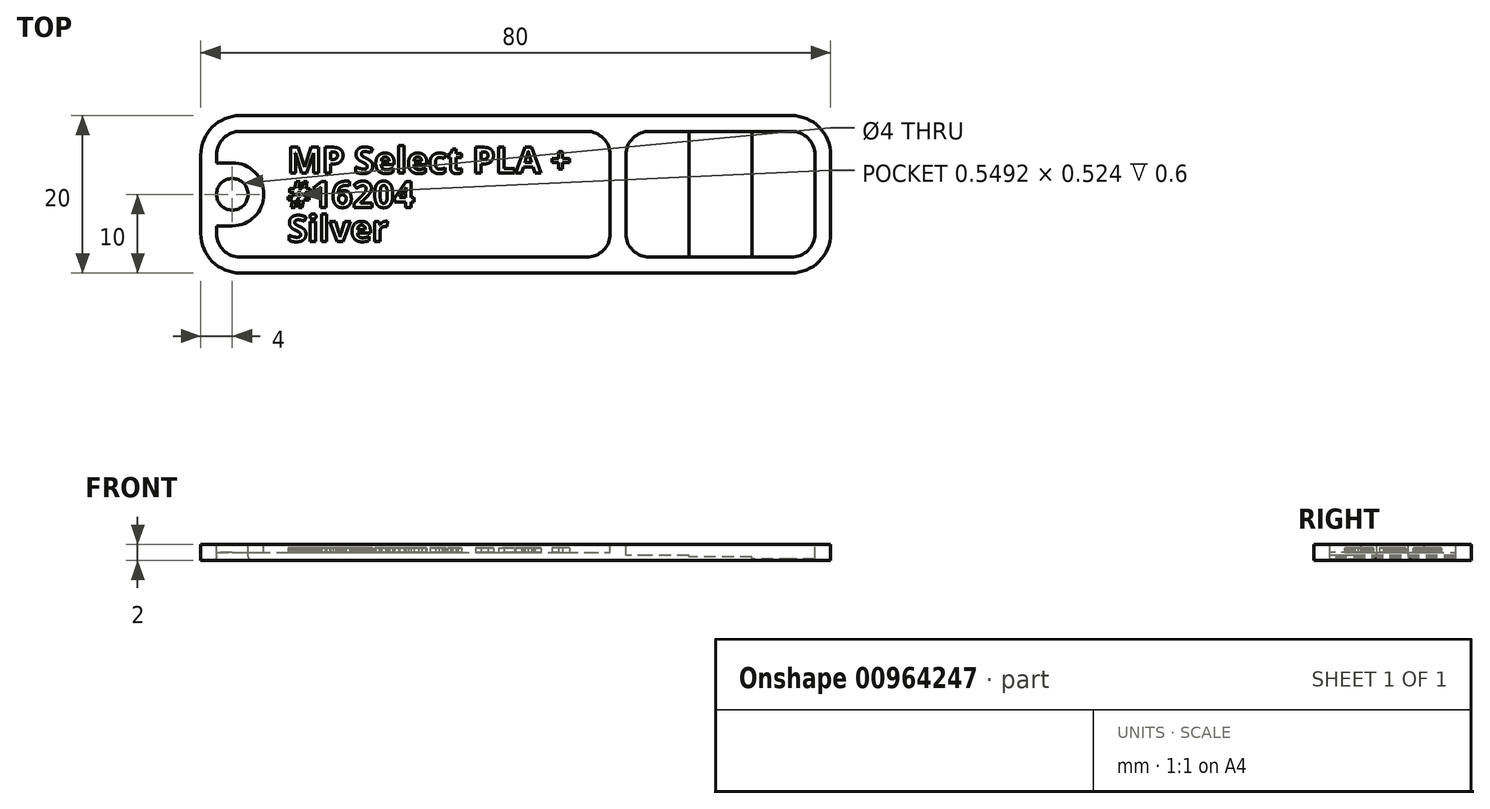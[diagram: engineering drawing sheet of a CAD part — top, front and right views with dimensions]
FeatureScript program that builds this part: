
annotation { "Feature Type Name" : "Feature", "Feature Type Description" : "" }
export const myFeature = defineFeature(function(context is Context, id is Id, definition is map)
    precondition{}
    {
        {
            var Q0;
            Q0=qCreatedBy(makeId("Top.planeOp"),FACE);
            var sketch = newSketch(context, id + "F0", { "sketchPlane" : qUnion([Q0])});
            skLineSegment(sketch, "E0.bottom", {"start": v(35, 10) * mm, "end": v(-35, 10) * mm});
            skLineSegment(sketch, "E0.top", {"start": v(35, -10) * mm, "end": v(-35, -10) * mm});
            skLineSegment(sketch, "E0.left", {"start": v(40, 5) * mm, "end": v(40, -5) * mm});
            skLineSegment(sketch, "E0.right", {"start": v(-40, 5) * mm, "end": v(-40, -5) * mm});
            skPoint(sketch, "E0.middle", {"position": v(0, 0) * mm});
            skPoint(sketch, "E1.visualSharp", {"position": v(-40, 10) * mm});
            skArc(sketch, "E1.filletArc", {"start": v(-35, 10) * mm, "mid": v(-38.54, 8.54) * mm, "end": v(-40, 5) * mm});
            skPoint(sketch, "E2.visualSharp", {"position": v(40, 10) * mm});
            skArc(sketch, "E2.filletArc", {"start": v(40, 5) * mm, "mid": v(38.54, 8.54) * mm, "end": v(35, 10) * mm});
            skPoint(sketch, "E3.visualSharp", {"position": v(40, -10) * mm});
            skArc(sketch, "E3.filletArc", {"start": v(35, -10) * mm, "mid": v(38.54, -8.54) * mm, "end": v(40, -5) * mm});
            skPoint(sketch, "E4.visualSharp", {"position": v(-40, -10) * mm});
            skArc(sketch, "E4.filletArc", {"start": v(-40, -5) * mm, "mid": v(-38.54, -8.54) * mm, "end": v(-35, -10) * mm});
            skSolve(sketch);
        }
        {
            var Q0;
            Q0=qSketchRegion(id+"F0",true);
            extrude(context, id + "F1", {"entities" : qUnion([Q0]), "offsetDistance" : 25 * mm, "depth" : 2 * mm});
        }
        {
            var Q0;
            Q0=makeQuery(id+"F1.opExtrude","CAP_FACE",FACE,{"disambiguationData":[OSD([sQuery(id+"F0.wireOp",EDGE,"E0.bottom"),sQuery(id+"F0.wireOp",EDGE,"E0.top"),sQuery(id+"F0.wireOp",EDGE,"E0.left"),sQuery(id+"F0.wireOp",EDGE,"E0.right"),sQuery(id+"F0.wireOp",EDGE,"E1.filletArc"),sQuery(id+"F0.wireOp",EDGE,"E2.filletArc"),sQuery(id+"F0.wireOp",EDGE,"E3.filletArc"),sQuery(id+"F0.wireOp",EDGE,"E4.filletArc")])],"isStart":false});
            var sketch = newSketch(context, id + "F2", { "sketchPlane" : qUnion([Q0])});
            skLineSegment(sketch, "E5.0", {"start": v(38, -5) * mm, "end": v(38, 5) * mm});
            skArc(sketch, "E5.1", {"start": v(35, -8) * mm, "mid": v(37.12, -7.12) * mm, "end": v(38, -5) * mm});
            skArc(sketch, "E5.2", {"start": v(38, 5) * mm, "mid": v(37.12, 7.12) * mm, "end": v(35, 8) * mm});
            skLineSegment(sketch, "E5.3", {"start": v(-35, -8) * mm, "end": v(9, -8) * mm});
            skLineSegment(sketch, "E5.4", {"start": v(35, 8) * mm, "end": v(17, 8) * mm});
            skArc(sketch, "E5.5", {"start": v(-35, 8) * mm, "mid": v(-37.12, 7.12) * mm, "end": v(-38, 5) * mm});
            skArc(sketch, "E5.7", {"start": v(-38, -5) * mm, "mid": v(-37.12, -7.12) * mm, "end": v(-35, -8) * mm});
            skCircle(sketch, "E6", {"center": v(-36, 0) * mm, "radius": 2 * mm, "construction": true});
            skArc(sketch, "E7.0", {"start": v(-36, -4) * mm, "mid": v(-32, 0) * mm, "end": v(-36, 4) * mm});
            skLineSegment(sketch, "E8", {"start": v(-38, -5) * mm, "end": v(-38, -4) * mm});
            skLineSegment(sketch, "E9", {"start": v(-36, 4) * mm, "end": v(-38, 4) * mm});
            skLineSegment(sketch, "E10", {"start": v(-36, -4) * mm, "end": v(-38, -4) * mm});
            skLineSegment(sketch, "E11.trimOffspring", {"start": v(-38, 4) * mm, "end": v(-38, 5) * mm});
            skArc(sketch, "E12", {"start": v(17, 8) * mm, "mid": v(14.88, 7.12) * mm, "end": v(14, 5) * mm});
            skArc(sketch, "E13", {"start": v(14, -5) * mm, "mid": v(14.88, -7.12) * mm, "end": v(17, -8) * mm});
            skLineSegment(sketch, "E14", {"start": v(14, -5) * mm, "end": v(14, 5) * mm});
            skArc(sketch, "E15", {"start": v(12, 5) * mm, "mid": v(11.12, 7.12) * mm, "end": v(9, 8) * mm});
            skArc(sketch, "E16", {"start": v(12, -5) * mm, "mid": v(11.12, -7.12) * mm, "end": v(9, -8) * mm});
            skLineSegment(sketch, "E17", {"start": v(12, -5) * mm, "end": v(12, 5) * mm});
            skLineSegment(sketch, "E18.trimOffspring", {"start": v(9, 8) * mm, "end": v(-35, 8) * mm});
            skLineSegment(sketch, "E19.trimOffspring", {"start": v(17, -8) * mm, "end": v(35, -8) * mm});
            skSolve(sketch);
        }
        {
            var Q0;
            Q0=qSketchRegion(id+"F2",true);
            extrude(context, id + "F3", {"entities" : qUnion([Q0]), "operationType" : NewBodyOperationType.REMOVE, "oppositeDirection" : true, "offsetDistance" : 25 * mm, "depth" : 1 * mm});
        }
        {
            var Q0;
            Q0=makeQuery(id+"F1.opExtrude","CAP_FACE",FACE,{"disambiguationData":[OSD([sQuery(id+"F0.wireOp",EDGE,"E0.bottom"),sQuery(id+"F0.wireOp",EDGE,"E0.top"),sQuery(id+"F0.wireOp",EDGE,"E0.left"),sQuery(id+"F0.wireOp",EDGE,"E0.right"),sQuery(id+"F0.wireOp",EDGE,"E1.filletArc"),sQuery(id+"F0.wireOp",EDGE,"E2.filletArc"),sQuery(id+"F0.wireOp",EDGE,"E3.filletArc"),sQuery(id+"F0.wireOp",EDGE,"E4.filletArc")])],"isStart":false});
            var sketch = newSketch(context, id + "F4", { "sketchPlane" : qUnion([Q0])});
            skCircle(sketch, "E20.0", {"center": v(-36, 0) * mm, "radius": 2 * mm});
            skSolve(sketch);
        }
        {
            var Q0;
            Q0=qSketchRegion(id+"F4",true);
            extrude(context, id + "F5", {"entities" : qUnion([Q0]), "operationType" : NewBodyOperationType.REMOVE, "endBound" : BoundingType.THROUGH_ALL, "oppositeDirection" : true, "depth" : 25 * mm});
        }
        {
            var Q0;
            Q0=makeQuery(id+"F5.boolean.opBoolean","COPY",EDGE,{"derivedFrom":makeQuery(id+"F5.opExtrude","CAP_EDGE",EDGE,{"disambiguationData":[OSD([sQuery(id+"F4.wireOp",EDGE,"E20.0")])],"isStart":true})});
            var Q1;
            Q1=makeQuery(id+"F5.boolean.opBoolean","INTERSECT",EDGE,{"derivedFrom":[makeQuery(id+"F1.opExtrude","CAP_FACE",FACE,{"disambiguationData":[OSD([sQuery(id+"F0.wireOp",EDGE,"E0.bottom"),sQuery(id+"F0.wireOp",EDGE,"E0.top"),sQuery(id+"F0.wireOp",EDGE,"E0.left"),sQuery(id+"F0.wireOp",EDGE,"E0.right"),sQuery(id+"F0.wireOp",EDGE,"E1.filletArc"),sQuery(id+"F0.wireOp",EDGE,"E2.filletArc"),sQuery(id+"F0.wireOp",EDGE,"E3.filletArc"),sQuery(id+"F0.wireOp",EDGE,"E4.filletArc")])],"isStart":true}),makeQuery(id+"F5.opExtrude","SWEPT_FACE",FACE,{"disambiguationData":[OSD([sQuery(id+"F4.wireOp",EDGE,"E20.0")])]})]});
            fillet(context, id + "F6", {"entities" : qUnion([Q0, Q1]), "radius" : .5 * mm, "tangentPropagation" : true, "allowEdgeOverflow" : false});
        }
        {
            var Q0;
            Q0=makeQuery(id+"F3.boolean.opBoolean","COPY",FACE,{"derivedFrom":makeQuery(id+"F3.opExtrude","CAP_FACE",FACE,{"disambiguationData":[OSD([sQuery(id+"F2.wireOp",EDGE,"E5.0"),sQuery(id+"F2.wireOp",EDGE,"E5.1"),sQuery(id+"F2.wireOp",EDGE,"E5.2"),sQuery(id+"F2.wireOp",EDGE,"E5.4"),sQuery(id+"F2.wireOp",EDGE,"E12"),sQuery(id+"F2.wireOp",EDGE,"E13"),sQuery(id+"F2.wireOp",EDGE,"E14"),sQuery(id+"F2.wireOp",EDGE,"E19.trimOffspring")])],"isStart":false})});
            extrude(context, id + "F7", {"entities" : qUnion([Q0]), "operationType" : NewBodyOperationType.REMOVE, "oppositeDirection" : true, "offsetDistance" : 25 * mm, "depth" : 0.4 * mm});
        }
        {
            var Q0;
            Q0=makeQuery(id+"F7.boolean.opBoolean","COPY",FACE,{"derivedFrom":makeQuery(id+"F7.opExtrude","CAP_FACE",FACE,{"disambiguationData":[OSD([sQuery(id+"F2.wireOp",EDGE,"E5.0"),sQuery(id+"F2.wireOp",EDGE,"E5.1"),sQuery(id+"F2.wireOp",EDGE,"E5.2"),sQuery(id+"F2.wireOp",EDGE,"E5.4"),sQuery(id+"F2.wireOp",EDGE,"E12"),sQuery(id+"F2.wireOp",EDGE,"E13"),sQuery(id+"F2.wireOp",EDGE,"E14"),sQuery(id+"F2.wireOp",EDGE,"E19.trimOffspring")])],"isStart":false})});
            var sketch = newSketch(context, id + "F8", { "sketchPlane" : qUnion([Q0])});
            skArc(sketch, "E21.0.0", {"start": v(35, -8) * mm, "mid": v(37.12, -7.12) * mm, "end": v(38, -5) * mm});
            skLineSegment(sketch, "E21.0.1", {"start": v(38, -5) * mm, "end": v(38, 5) * mm});
            skArc(sketch, "E21.0.2", {"start": v(38, 5) * mm, "mid": v(37.12, 7.12) * mm, "end": v(35, 8) * mm});
            skLineSegment(sketch, "E21.0.3", {"start": v(35, 8) * mm, "end": v(22, 8) * mm});
            skLineSegment(sketch, "E21.0.7", {"start": v(22, -8) * mm, "end": v(35, -8) * mm});
            skLineSegment(sketch, "E22", {"start": v(22, 8) * mm, "end": v(22, -8) * mm});
            skPoint(sketch, "E21.0.4.start.orphan", {"position": v(17, 8) * mm});
            skPoint(sketch, "E21.0.5.start.orphan", {"position": v(14, 5) * mm});
            skPoint(sketch, "E21.0.6.start.orphan", {"position": v(14, -5) * mm});
            skPoint(sketch, "E23.orphan", {"position": v(17, -8) * mm});
            skSolve(sketch);
        }
        {
            var Q0;
            Q0=qSketchRegion(id+"F8",true);
            extrude(context, id + "F9", {"entities" : qUnion([Q0]), "operationType" : NewBodyOperationType.REMOVE, "oppositeDirection" : true, "offsetDistance" : 25 * mm, "depth" : 0.2 * mm});
        }
        {
            var Q0;
            Q0=makeQuery(id+"F9.boolean.opBoolean","COPY",FACE,{"derivedFrom":makeQuery(id+"F9.opExtrude","CAP_FACE",FACE,{"disambiguationData":[OSD([sQuery(id+"F8.wireOp",EDGE,"E21.0.0"),sQuery(id+"F8.wireOp",EDGE,"E21.0.1"),sQuery(id+"F8.wireOp",EDGE,"E21.0.2"),sQuery(id+"F8.wireOp",EDGE,"E21.0.3"),sQuery(id+"F8.wireOp",EDGE,"E21.0.7"),sQuery(id+"F8.wireOp",EDGE,"E22")])],"isStart":false})});
            var sketch = newSketch(context, id + "F10", { "sketchPlane" : qUnion([Q0])});
            skLineSegment(sketch, "E24.0.0", {"start": v(35, 8) * mm, "end": v(30, 8) * mm});
            skLineSegment(sketch, "E24.0.2", {"start": v(30, -8) * mm, "end": v(35, -8) * mm});
            skArc(sketch, "E24.0.3", {"start": v(35, -8) * mm, "mid": v(37.12, -7.12) * mm, "end": v(38, -5) * mm});
            skLineSegment(sketch, "E24.0.4", {"start": v(38, -5) * mm, "end": v(38, 5) * mm});
            skArc(sketch, "E24.0.5", {"start": v(38, 5) * mm, "mid": v(37.12, 7.12) * mm, "end": v(35, 8) * mm});
            skLineSegment(sketch, "E25", {"start": v(30, 8) * mm, "end": v(30, -8) * mm});
            skPoint(sketch, "E24.0.1.end.orphan", {"position": v(22, -8) * mm});
            skPoint(sketch, "E26.orphan", {"position": v(22, 8) * mm});
            skSolve(sketch);
        }
        {
            var Q0;
            Q0=makeQuery(id+"F10.imprint","IMPRINT",FACE,{"disambiguationData":[TD([[makeQuery(id+"F10.imprint","IMPRINT",EDGE,{"derivedFrom":sQuery(id+"F10.wireOp",EDGE,"E24.0.0")}),1.0]])]});
            extrude(context, id + "F11", {"entities" : qUnion([Q0]), "operationType" : NewBodyOperationType.REMOVE, "oppositeDirection" : true, "offsetDistance" : 25 * mm, "depth" : 0.2 * mm});
        }
        {
            var Q0;
            Q0=makeQuery(id+"F3.boolean.opBoolean","COPY",FACE,{"derivedFrom":makeQuery(id+"F3.opExtrude","CAP_FACE",FACE,{"disambiguationData":[OSD([sQuery(id+"F2.wireOp",EDGE,"E5.3"),sQuery(id+"F2.wireOp",EDGE,"E5.5"),sQuery(id+"F2.wireOp",EDGE,"E5.7"),sQuery(id+"F2.wireOp",EDGE,"E7.0"),sQuery(id+"F2.wireOp",EDGE,"E8"),sQuery(id+"F2.wireOp",EDGE,"E9"),sQuery(id+"F2.wireOp",EDGE,"E10"),sQuery(id+"F2.wireOp",EDGE,"E11.trimOffspring"),sQuery(id+"F2.wireOp",EDGE,"E15"),sQuery(id+"F2.wireOp",EDGE,"E16"),sQuery(id+"F2.wireOp",EDGE,"E17"),sQuery(id+"F2.wireOp",EDGE,"E18.trimOffspring")])],"isStart":false})});
            var sketch = newSketch(context, id + "F12", { "sketchPlane" : qUnion([Q0])});
            skText(sketch, "E27", { "text": "MP Select PLA +", "fontName": "OpenSans-Bold.ttf"});
            skText(sketch, "E28", { "text": "#16204", "fontName": "OpenSans-Bold.ttf"});
            skText(sketch, "E29", { "text": "Silver", "fontName": "OpenSans-Bold.ttf"});
            skLineSegment(sketch, "E30", {"start": v(-27.83, 1.67) * mm, "end": v(-27.83, 2.67) * mm, "construction": true});
            skLineSegment(sketch, "E31", {"start": v(-26.66, -2.67) * mm, "end": v(-26.66, -1.67) * mm, "construction": true});
            skLineSegment(sketch, "E32.bottom", {"start": v(-31, 7) * mm, "end": v(10, 7) * mm, "construction": true});
            skLineSegment(sketch, "E32.top", {"start": v(-31, -7) * mm, "end": v(10, -7) * mm, "construction": true});
            skLineSegment(sketch, "E32.left", {"start": v(-31, 7) * mm, "end": v(-31, -7) * mm, "construction": true});
            skLineSegment(sketch, "E32.right", {"start": v(10, 7) * mm, "end": v(10, -7) * mm, "construction": true});
            skLineSegment(sketch, "E33", {"start": v(-13.47, 7) * mm, "end": v(-13.47, 8) * mm, "construction": true});
            skLineSegment(sketch, "E34", {"start": v(-13.67, -7) * mm, "end": v(-13.67, -8) * mm, "construction": true});
            skLineSegment(sketch, "E35", {"start": v(-32, 0) * mm, "end": v(-31, 0) * mm, "construction": true});
            skPoint(sketch, "E35.startSnap0", {"position": v(-31, 0) * mm});
            skLineSegment(sketch, "E36", {"start": v(-29, 4.33) * mm, "end": v(-31, 4.33) * mm, "construction": true});
            skLineSegment(sketch, "E37", {"start": v(10, 1.23) * mm, "end": v(12, 1.23) * mm, "construction": true});
            skLineSegment(sketch, "E38", {"start": v(-29, -0.54) * mm, "end": v(-31, -0.54) * mm, "construction": true});
            skLineSegment(sketch, "E39", {"start": v(-29, -4.33) * mm, "end": v(-31, -4.33) * mm, "construction": true});
            skLineSegment(sketch, "E40", {"start": v(-25.76, 6) * mm, "end": v(-25.76, 7) * mm, "construction": true});
            skLineSegment(sketch, "E41", {"start": v(-26.93, -6) * mm, "end": v(-26.93, -7) * mm, "construction": true});
            const initialGuessF12  = {"E27": [-0.029, 0.00267, 1, 0, 0.00333], "E28": [-0.029, -0.00167, 1, 0, 0.00333], "E29": [-0.029, -0.006, 1, 0, 0.00333]};
            skSetInitialGuess(sketch, initialGuessF12);
            skSolve(sketch);
        }
        {
            var Q0;
            Q0=qSketchRegion(id+"F12",true);
            extrude(context, id + "F13", {"entities" : qUnion([Q0]), "operationType" : NewBodyOperationType.ADD, "depth" : 0.6 * mm, "offsetDistance" : 25 * mm});
        }
    });
